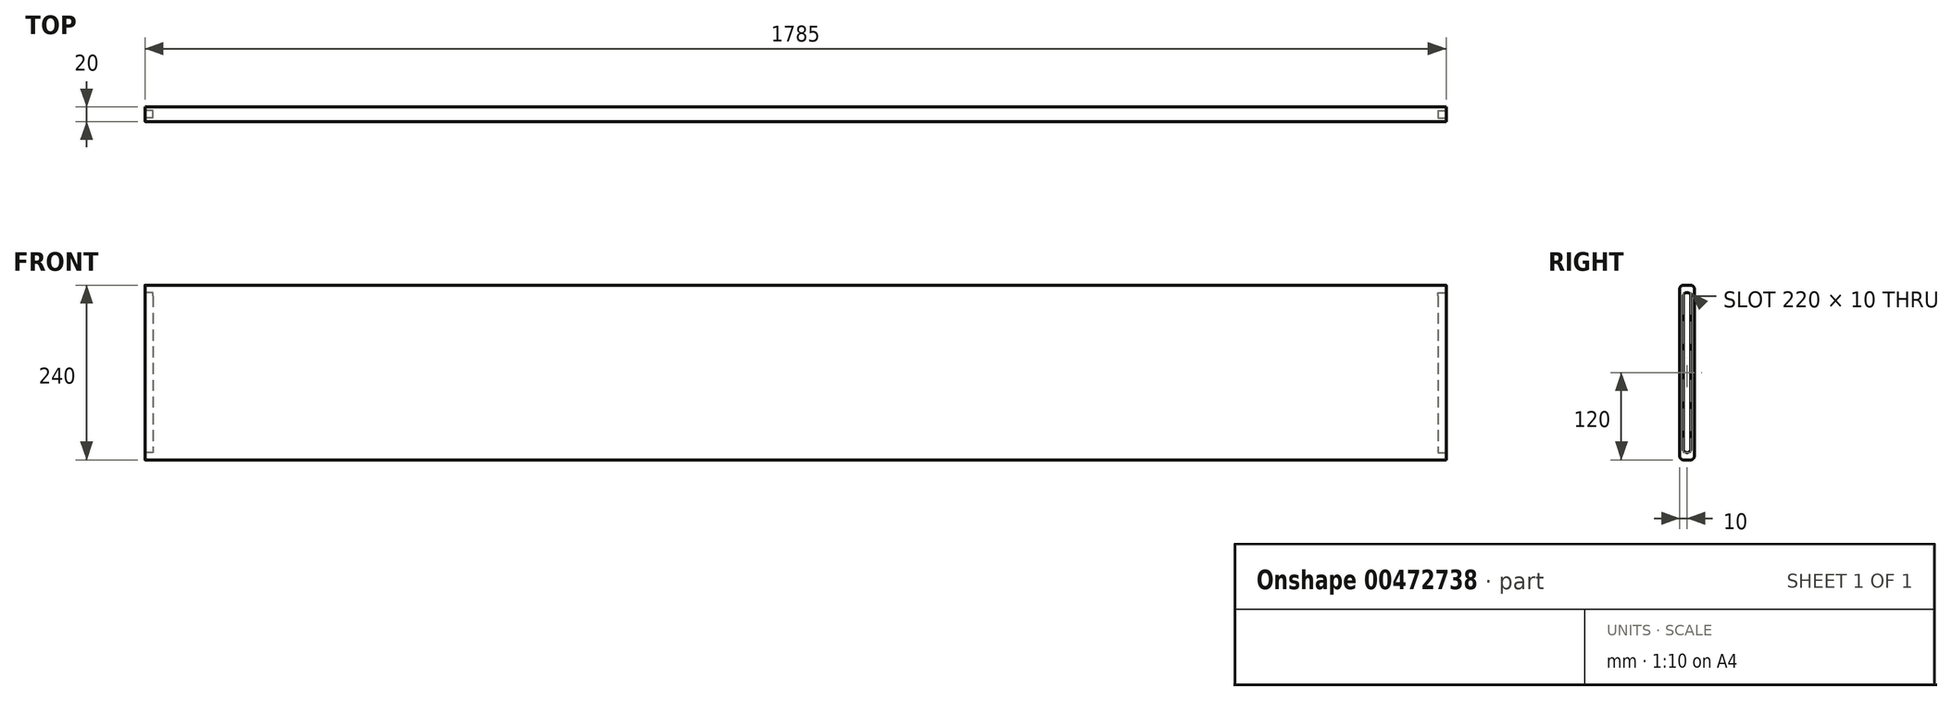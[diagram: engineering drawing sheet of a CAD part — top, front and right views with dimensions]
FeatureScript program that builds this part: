
annotation { "Feature Type Name" : "Feature", "Feature Type Description" : "" }
export const myFeature = defineFeature(function(context is Context, id is Id, definition is map)
    precondition{}
    {
        {
            var Q0;
            Q0=qCreatedBy(makeId("Front.planeOp"),FACE);
            var sketch = newSketch(context, id + "F0", { "sketchPlane" : qUnion([Q0])});
            skLineSegment(sketch, "E0.bottom", {"start": v(-892.5, 120) * mm, "end": v(892.5, 120) * mm});
            skLineSegment(sketch, "E0.top", {"start": v(-892.5, -120) * mm, "end": v(892.5, -120) * mm});
            skLineSegment(sketch, "E0.left", {"start": v(-892.5, 120) * mm, "end": v(-892.5, -120) * mm});
            skLineSegment(sketch, "E0.right", {"start": v(892.5, 120) * mm, "end": v(892.5, -120) * mm});
            skLineSegment(sketch, "E1", {"start": v(892.5, 0) * mm, "end": v(-892.5, 0) * mm, "construction": true});
            skSolve(sketch);
        }
        {
            var Q0;
            Q0 = qSketchRegion(id + "F0", true);
            extrude(context, id + "F1", {"entities" : qUnion([Q0]), "depth" : 20 * mm});
        }
        {
            var Q0;
            Q0=makeQuery(id+"F1.opExtrude","SWEPT_FACE",FACE,{"disambiguationData":[OSD([sQuery(id+"F0.wireOp",EDGE,"E0.left")])]});
            var sketch = newSketch(context, id + "F2", { "sketchPlane" : qUnion([Q0])});
            skLineSegment(sketch, "E2", {"start": v(10, 120) * mm, "end": v(10, -120) * mm, "construction": true});
            skLineSegment(sketch, "E3", {"start": v(0, 0) * mm, "end": v(20, 0) * mm, "construction": true});
            skArc(sketch, "E4", {"start": v(5, -105) * mm, "mid": v(10, -110) * mm, "end": v(15, -105) * mm});
            skArc(sketch, "E5.MirrorC", {"start": v(5, 105) * mm, "mid": v(10, 110) * mm, "end": v(15, 105) * mm});
            skLineSegment(sketch, "E6", {"start": v(15, 105) * mm, "end": v(15, -105) * mm});
            skLineSegment(sketch, "E7.MirrorCS", {"start": v(5, 105) * mm, "end": v(5, -105) * mm});
            skSolve(sketch);
        }
        {
            var Q0;
            Q0 = qSketchRegion(id + "F2", true);
            extrude(context, id + "F3", {"entities" : qUnion([Q0]), "operationType" : NewBodyOperationType.REMOVE, "oppositeDirection" : true, "depth" : 11 * mm, "offsetDistance" : 25 * mm});
        }
        {
            var Q0;
            Q0=makeQuery(id+"F1.opExtrude","SWEPT_FACE",FACE,{"disambiguationData":[OSD([sQuery(id+"F0.wireOp",EDGE,"E0.right")])]});
            var sketch = newSketch(context, id + "F4", { "sketchPlane" : qUnion([Q0])});
            skLineSegment(sketch, "E8", {"start": v(-10, 120) * mm, "end": v(-10, -120) * mm, "construction": true});
            skLineSegment(sketch, "E9", {"start": v(-20, 0) * mm, "end": v(0, 0) * mm, "construction": true});
            skArc(sketch, "E10", {"start": v(-5, 105) * mm, "mid": v(-10, 110) * mm, "end": v(-15, 105) * mm});
            skArc(sketch, "E11.MirrorC", {"start": v(-5, -105) * mm, "mid": v(-10, -110) * mm, "end": v(-15, -105) * mm});
            skLineSegment(sketch, "E12", {"start": v(-15, 105) * mm, "end": v(-15, -105) * mm});
            skLineSegment(sketch, "E13.MirrorCS", {"start": v(-5, 105) * mm, "end": v(-5, -105) * mm});
            skSolve(sketch);
        }
        {
            var Q0;
            Q0 = qSketchRegion(id + "F4", true);
            extrude(context, id + "F5", {"entities" : qUnion([Q0]), "operationType" : NewBodyOperationType.REMOVE, "oppositeDirection" : true, "depth" : 11 * mm, "offsetDistance" : 25 * mm});
        }
        {
            var Q0;
            Q0=makeQuery(id+"F1.opExtrude","CAP_EDGE",EDGE,{"disambiguationData":[OSD([sQuery(id+"F0.wireOp",EDGE,"E0.bottom")])],"isStart":true});
            var Q1;
            Q1=makeQuery(id+"F1.opExtrude","CAP_EDGE",EDGE,{"disambiguationData":[OSD([sQuery(id+"F0.wireOp",EDGE,"E0.bottom")])],"isStart":false});
            var Q2;
            Q2=makeQuery(id+"F1.opExtrude","CAP_EDGE",EDGE,{"disambiguationData":[OSD([sQuery(id+"F0.wireOp",EDGE,"E0.top")])],"isStart":true});
            var Q3;
            Q3=makeQuery(id+"F1.opExtrude","CAP_EDGE",EDGE,{"disambiguationData":[OSD([sQuery(id+"F0.wireOp",EDGE,"E0.top")])],"isStart":false});
            fillet(context, id + "F6", {"entities" : qUnion([Q0, Q1, Q2, Q3]), "radius" : 5 * mm, "tangentPropagation" : true, "allowEdgeOverflow" : false});
        }
    });
